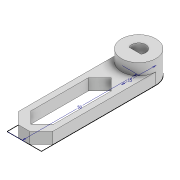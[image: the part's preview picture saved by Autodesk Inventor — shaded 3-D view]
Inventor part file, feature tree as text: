
AUTODESK INVENTOR PART (.ipt)
format: ipt  version: 2020.3 (Build 243373000, 373)  size: 116,736 bytes
history: native  units: mm
features: extrude x3, sketch x2, chamfer x2
ambient origin geometry x8: Origin, YZ Plane, XZ Plane, XY Plane, X Axis, Y Axis, Z Axis, Center Point
bodies: Solid1 (feature_tree)
feature tree (7):
  sketch  "Sketch1"  dims[d1=15.0mm d2=50.0mm]
  extrude  "Extrusion1"  Depth=15.0mm
  extrude  "Extrusion2"  Depth=5.0mm TaperAngle=0.0deg
  chamfer  "Chamfer1"  Distance=5.0mm Angle=45.0deg
  extrude  "Extrusion3"  Depth=5.0mm TaperAngle=0.0deg
  chamfer  "Chamfer2"  Distance=10.0mm
  sketch  "Sketch3"  dims[d3=10.0mm d4=0.0mm d5=5.0mm d6=0.0mm d7=5.0mm d8=2.0mm d9=45.0deg d10=5.5mm d11=0.0mm d13=10.0mm d14=30.0mm d15=3.0mm d16=5.0mm d17=2.0mm d18=45.0deg d19=0.872665mm]
